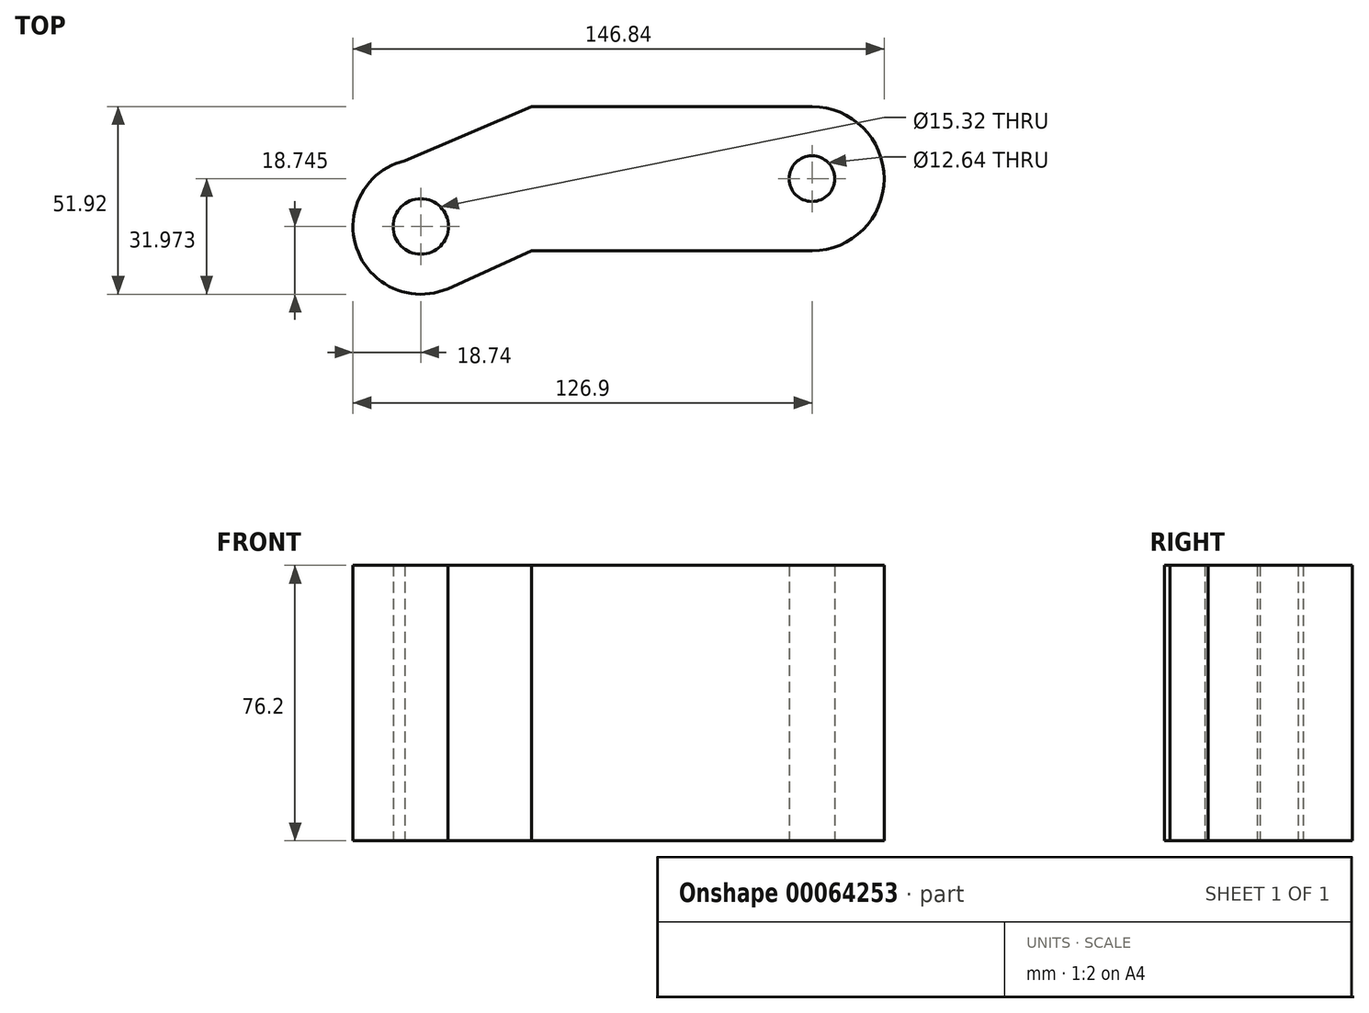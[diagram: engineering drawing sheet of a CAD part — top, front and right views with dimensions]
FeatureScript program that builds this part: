
annotation { "Feature Type Name" : "Feature", "Feature Type Description" : "" }
export const myFeature = defineFeature(function(context is Context, id is Id, definition is map)
    precondition{}
    {
        {
            var Q0;
            Q0=qCreatedBy(makeId("Top.planeOp"),FACE);
            var sketch = newSketch(context, id + "F0", { "sketchPlane" : qUnion([Q0])});
            skLineSegment(sketch, "E0.bottom", {"start": v(0, 0) * mm, "end": v(-77.58, 0) * mm});
            skLineSegment(sketch, "E0.top", {"start": v(0, 39.89) * mm, "end": v(-77.58, 39.89) * mm});
            skArc(sketch, "E1", {"start": v(0, 0) * mm, "mid": v(19.94, 19.94) * mm, "end": v(0, 39.89) * mm});
            skLineSegment(sketch, "E2", {"start": v(-77.58, 39.89) * mm, "end": v(-112.62, 24.92) * mm});
            skLineSegment(sketch, "E3", {"start": v(-77.58, 0) * mm, "end": v(-100.72, -10.49) * mm});
            skArc(sketch, "E4", {"start": v(-112.62, 24.92) * mm, "mid": v(-125.92, 0.74) * mm, "end": v(-100.72, -10.49) * mm});
            skCircle(sketch, "E5", {"center": v(-108.16, 6.72) * mm, "radius": 7.66 * mm});
            skCircle(sketch, "E6", {"center": v(0, 19.94) * mm, "radius": 6.32 * mm});
            skSolve(sketch);
        }
        {
            var Q0;
            Q0=makeQuery(id+"F0.imprint","IMPRINT",FACE,{"disambiguationData":[TD([[makeQuery(id+"F0.imprint","IMPRINT",EDGE,{"derivedFrom":sQuery(id+"F0.wireOp",EDGE,"E0.bottom")}),-1.0]])]});
            extrude(context, id + "F1", {"entities" : qUnion([Q0]), "depth" : 76.2 * mm});
        }
    });
